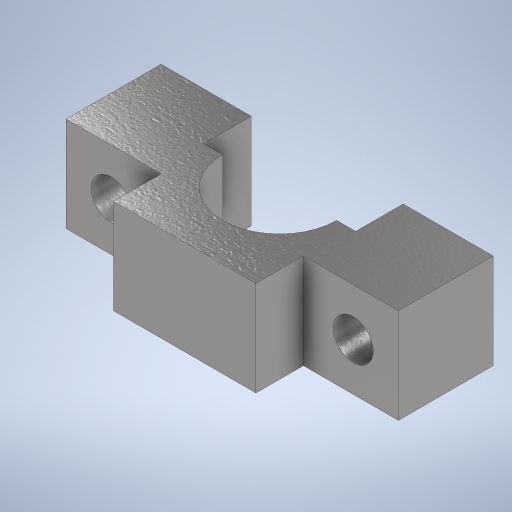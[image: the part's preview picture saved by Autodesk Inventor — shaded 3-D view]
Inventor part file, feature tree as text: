
AUTODESK INVENTOR PART (.ipt)
format: ipt  version: 2024 (Build 280153000, 153)  size: 311,808 bytes
history: native  units: mm
features: sketch x3, extrude x2, hole x1
ambient origin geometry x8: Origin, YZ Plane, XZ Plane, XY Plane, X Axis, Y Axis, Z Axis, Center Point
bodies: Volumenkörper1 (feature_tree)
feature tree (6):
  extrude  "Extrusion1"  Depth=5.0mm
  extrude  "Extrusion2"  Depth=10.0mm TaperAngle=0.0deg
  hole  "Bohrung1"  [1 undecoded]
  sketch  "Skizze1"  dims[d0=16.0mm d1=5.0mm]
  sketch  "Skizze2"  dims[d2=35.0mm d5=10.0mm d6=0.0mm]
  sketch  "Skizze3"  dims[d7=15.0mm d10=5.0mm d11=15.0mm d12=6.0mm d13=10.0mm d14=0.0mm d15=25.5mm d16=4.2mm d17=6.0mm d18=4.0mm d19=2.0mm d20=90.0deg d21=8.0mm d22=0.0mm]
note: 1 required parameter value undecoded (feature->parameter linkage not recoverable at this tier; creation-order binding heuristic only, values carry confidence <= 0.55)
